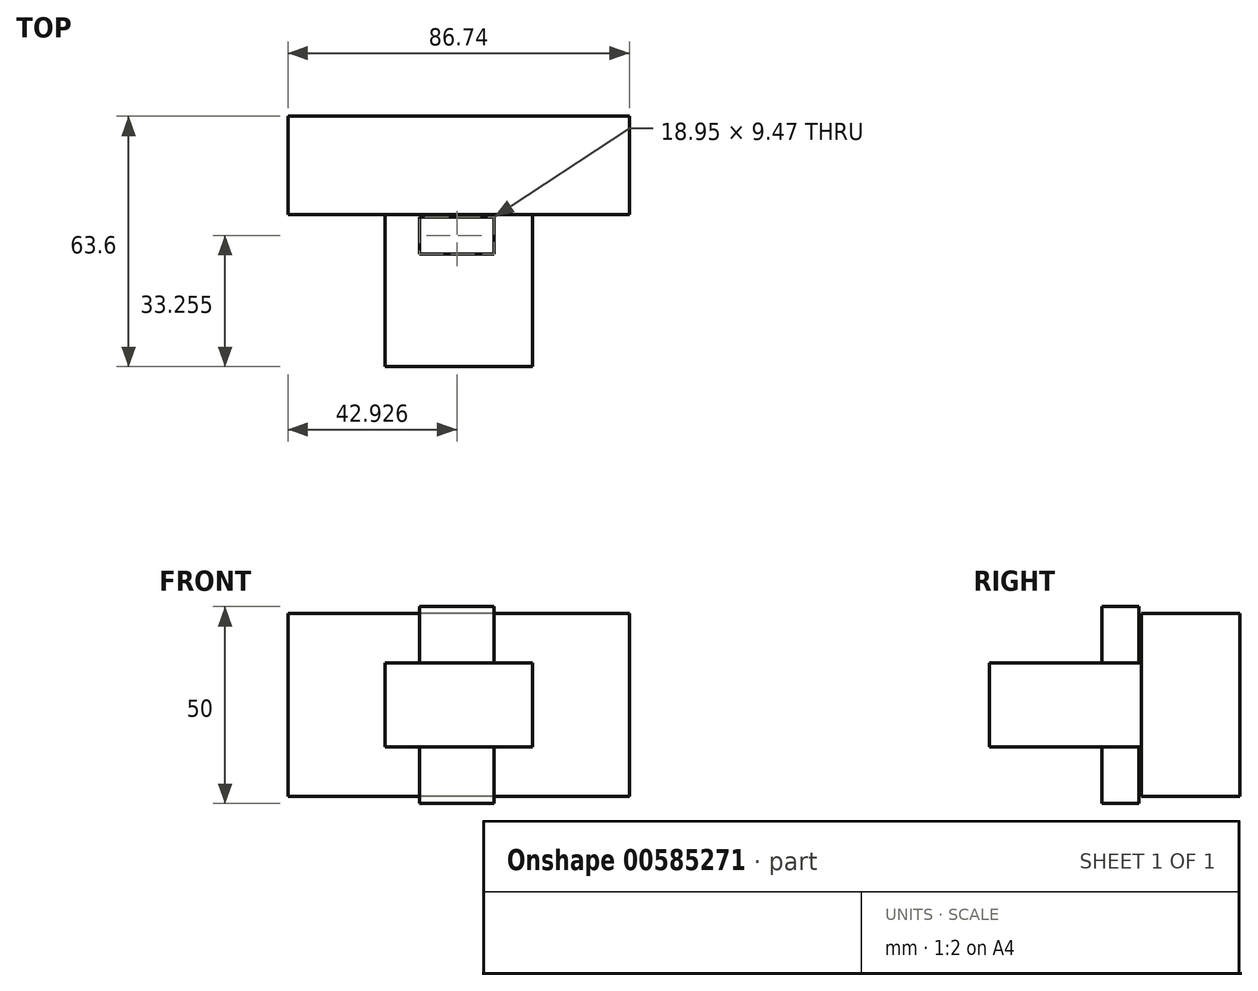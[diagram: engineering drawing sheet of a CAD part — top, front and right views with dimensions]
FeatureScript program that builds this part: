
annotation { "Feature Type Name" : "Feature", "Feature Type Description" : "" }
export const myFeature = defineFeature(function(context is Context, id is Id, definition is map)
    precondition{}
    {
        {
            var Q0;
            Q0=qCreatedBy(makeId("Front.planeOp"),FACE);
            var sketch = newSketch(context, id + "F0", { "sketchPlane" : qUnion([Q0])});
            skLineSegment(sketch, "E0.bottom", {"start": v(43.37, -23.24) * mm, "end": v(-43.37, -23.24) * mm});
            skLineSegment(sketch, "E0.top", {"start": v(43.37, 23.24) * mm, "end": v(-43.37, 23.24) * mm});
            skLineSegment(sketch, "E0.left", {"start": v(43.37, -23.24) * mm, "end": v(43.37, 23.24) * mm});
            skLineSegment(sketch, "E0.right", {"start": v(-43.37, -23.24) * mm, "end": v(-43.37, 23.24) * mm});
            skPoint(sketch, "E0.middle", {"position": v(0, 0) * mm});
            skSolve(sketch);
        }
        {
            var Q0;
            Q0 = qSketchRegion(id + "F0", true);
            extrude(context, id + "F1", {"entities" : qUnion([Q0]), "depth" : 25 * mm, "offsetDistance" : 25 * mm});
        }
        {
            var Q0;
            Q0=qCreatedBy(makeId("Front.planeOp"),FACE);
            var sketch = newSketch(context, id + "F2", { "sketchPlane" : qUnion([Q0])});
            skLineSegment(sketch, "E1.bottom", {"start": v(-18.74, -10.62) * mm, "end": v(18.74, -10.62) * mm});
            skLineSegment(sketch, "E1.top", {"start": v(-18.74, 10.62) * mm, "end": v(18.74, 10.62) * mm});
            skLineSegment(sketch, "E1.left", {"start": v(-18.74, -10.62) * mm, "end": v(-18.74, 10.62) * mm});
            skLineSegment(sketch, "E1.right", {"start": v(18.74, -10.62) * mm, "end": v(18.74, 10.62) * mm});
            skPoint(sketch, "E1.middle", {"position": v(0, 0) * mm});
            skSolve(sketch);
        }
        {
            var Q0;
            Q0 = qSketchRegion(id + "F2", true);
            extrude(context, id + "F3", {"entities" : qUnion([Q0]), "operationType" : NewBodyOperationType.ADD, "depth" : 63.6 * mm, "offsetDistance" : 25 * mm});
        }
        {
            var Q0;
            Q0=qCreatedBy(makeId("Top.planeOp"),FACE);
            var sketch = newSketch(context, id + "F4", { "sketchPlane" : qUnion([Q0])});
            skLineSegment(sketch, "E2.bottom", {"start": v(-9.92, -25.6) * mm, "end": v(9.03, -25.6) * mm});
            skLineSegment(sketch, "E2.top", {"start": v(-9.92, -35.08) * mm, "end": v(9.03, -35.08) * mm});
            skLineSegment(sketch, "E2.left", {"start": v(-9.92, -25.6) * mm, "end": v(-9.92, -35.08) * mm});
            skLineSegment(sketch, "E2.right", {"start": v(9.03, -25.6) * mm, "end": v(9.03, -35.08) * mm});
            skSolve(sketch);
        }
        {
            var Q0;
            Q0 = qSketchRegion(id + "F4", true);
            extrude(context, id + "F5", {"entities" : qUnion([Q0]), "operationType" : NewBodyOperationType.ADD, "depth" : -25 * mm, "offsetDistance" : 25 * mm});
        }
        {
            var Q0;
            Q0 = qSketchRegion(id + "F4", true);
            extrude(context, id + "F6", {"entities" : qUnion([Q0]), "operationType" : NewBodyOperationType.ADD, "depth" : 25 * mm, "offsetDistance" : 25 * mm});
        }
    });
